# Revit family: QF-Storage_Tank-OptiPure-50G
name_source: partatom
category: Specialty Equipment
revit_build: Autodesk Revit 2017 (Build: 20160225_1515(x64)
units: mm (PartAtom-declared; Revit-internal decimal feet)

## family parameters
Always vertical = Yes
Cut with Voids When Loaded = No
OmniClass Number = 23.40.40.14
OmniClass Title = Food Service Equipment
Part Type = Normal
Room Calculation Point = No
Round Connector Dimension = Use Diameter
Shared = No
Work Plane-Based = No

## types (1)
- 50G
    Assembly Code = E1090300
    Case Material = Stainless Steel
    Connectors Material = White Nylon
    Description = WATER STORAGE TANK
    Filtered Water In = 0.5 "
    Filtered Water Supply Size = 1"
    Height = 51.81 "
    Keynote = 11400
    Length = 26.5 "
    Manufacturer = OPTIPURE
    Material = Black Plastic
    Model = 164-80051 - 50G TANK ASSY
    Plastic Tube = White Plastic
    Tank Material = Blue Plastic
    URL = WWW.OPTIPUREWATER.COM
    Valve Material = Plastic
    Width = 26.5 "

## geometry (parser evidence)
native form markers: Sweep x2
no freeform markers — native parametric forms only
